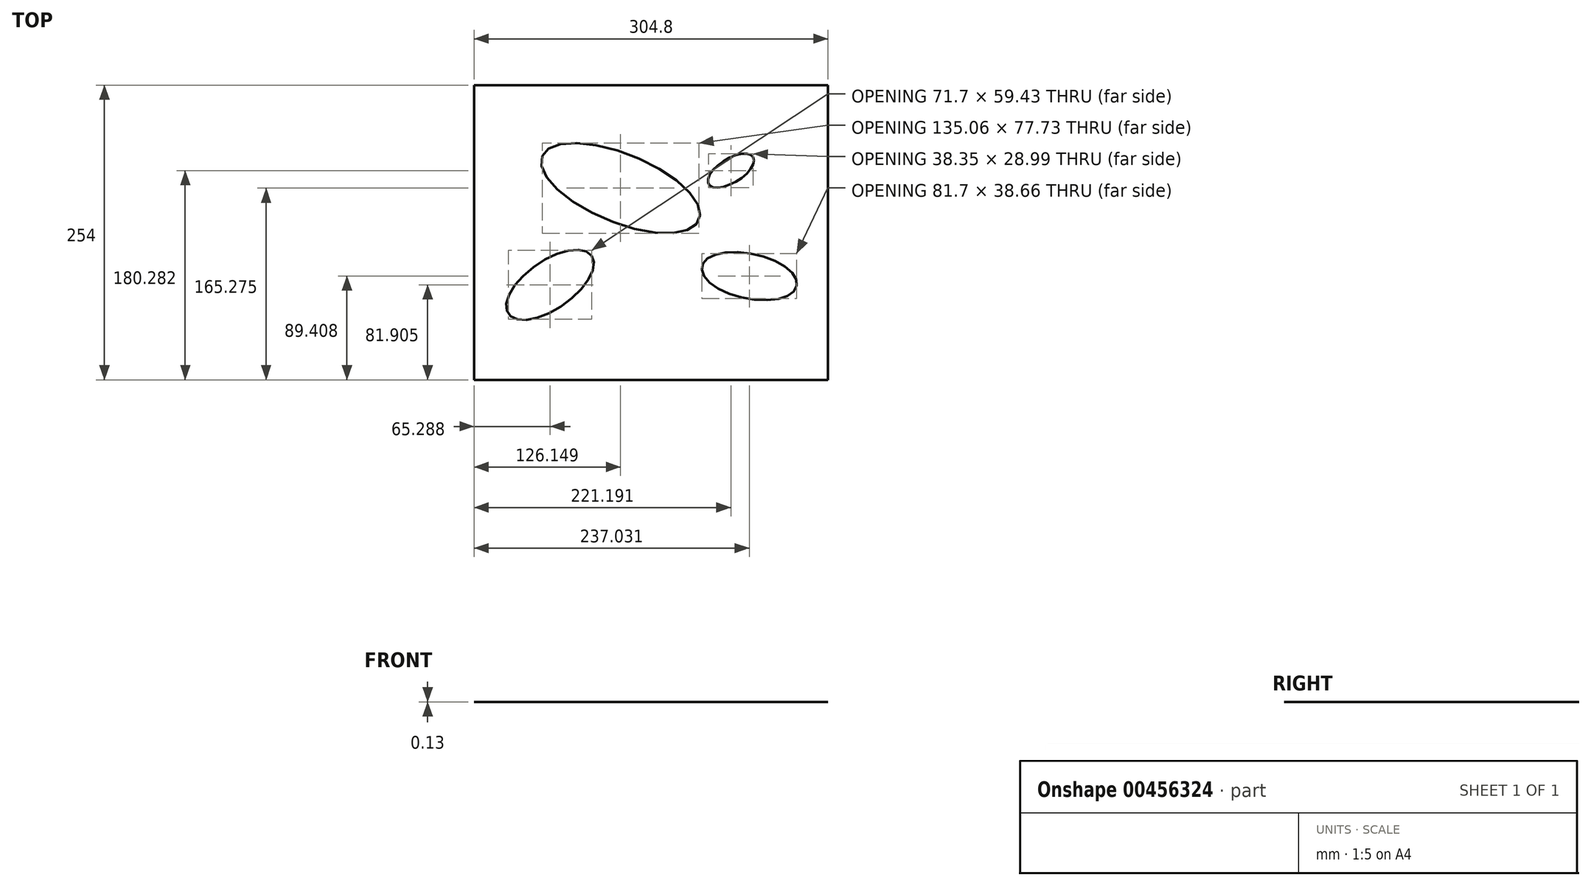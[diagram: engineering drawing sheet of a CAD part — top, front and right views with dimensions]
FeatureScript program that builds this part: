
annotation { "Feature Type Name" : "Feature", "Feature Type Description" : "" }
export const myFeature = defineFeature(function(context is Context, id is Id, definition is map)
    precondition{}
    {
        {
            var Q0;
            Q0=qCreatedBy(makeId("Top.planeOp"),FACE);
            var sketch = newSketch(context, id + "F0", { "sketchPlane" : qUnion([Q0])});
            skLineSegment(sketch, "E0", {"start": v(-152.4, 0) * mm, "end": v(152.4, 0) * mm, "construction": true});
            skLineSegment(sketch, "E1", {"start": v(0, 127) * mm, "end": v(0, -127) * mm, "construction": true});
            skPoint(sketch, "E2", {"position": v(0, 0) * mm});
            skPoint(sketch, "E3", {"position": v(-152.4, 127) * mm});
            skPoint(sketch, "E4.MirrorP", {"position": v(-152.4, -127) * mm});
            skPoint(sketch, "E5.MirrorP", {"position": v(152.4, 127) * mm});
            skPoint(sketch, "E6.MirrorP", {"position": v(152.4, -127) * mm});
            skLineSegment(sketch, "E7", {"start": v(-152.4, 127) * mm, "end": v(152.4, 127) * mm});
            skLineSegment(sketch, "E8", {"start": v(-152.4, 127) * mm, "end": v(-152.4, -127) * mm});
            skLineSegment(sketch, "E9", {"start": v(-152.4, -127) * mm, "end": v(152.4, -127) * mm});
            skLineSegment(sketch, "E10", {"start": v(152.4, -127) * mm, "end": v(152.4, 127) * mm});
            skPoint(sketch, "E11", {"position": v(-87.11, -45.1) * mm});
            skPoint(sketch, "E12", {"position": v(-26.25, 38.28) * mm});
            skPoint(sketch, "E13", {"position": v(84.63, -37.6) * mm});
            skPoint(sketch, "E14", {"position": v(68.8, 53.28) * mm});
            skEllipse(sketch, "E15", {"center": v(-87.11, -45.1) * mm, "majorRadius": 43.71 * mm, "minorRadius": 20.75 * mm, "majorAxis": v(0.82, 0.57)});
            skEllipse(sketch, "E16", {"center": v(-26.25, 38.28) * mm, "majorRadius": 72.92 * mm, "minorRadius": 29.64 * mm, "majorAxis": v(-0.93, 0.38)});
            skEllipse(sketch, "E17", {"center": v(68.8, 53.28) * mm, "majorRadius": 22.45 * mm, "minorRadius": 10.34 * mm, "majorAxis": v(0.85, 0.52)});
            skEllipse(sketch, "E18", {"center": v(84.63, -37.6) * mm, "majorRadius": 41.7 * mm, "minorRadius": 19.4 * mm, "majorAxis": v(0.98, -0.2)});
            skSolve(sketch);
        }
        {
            var Q0;
            Q0=makeQuery(id+"F0.imprint","IMPRINT",FACE,{"disambiguationData":[TD([[makeQuery(id+"F0.imprint","IMPRINT",EDGE,{"derivedFrom":sQuery(id+"F0.wireOp",EDGE,"E7")}),-1.0]])]});
            extrude(context, id + "F1", {"entities" : qUnion([Q0]), "depth" : 0.13 * mm});
        }
    });
